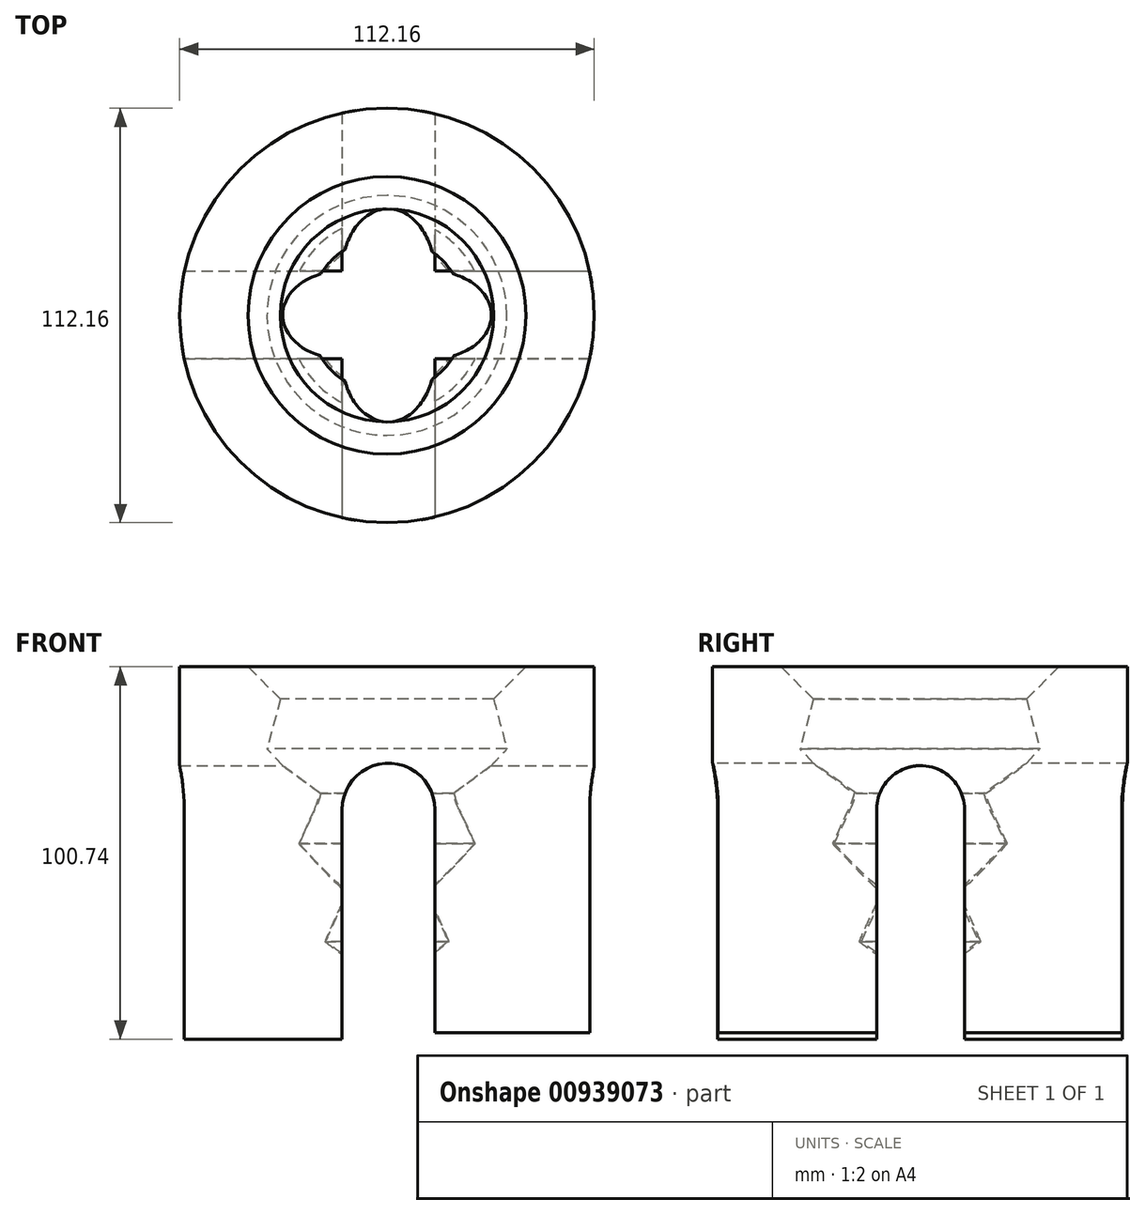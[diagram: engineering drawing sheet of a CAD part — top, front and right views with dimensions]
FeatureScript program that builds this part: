
annotation { "Feature Type Name" : "Feature", "Feature Type Description" : "" }
export const myFeature = defineFeature(function(context is Context, id is Id, definition is map)
    precondition{}
    {
        {
            var Q0;
            Q0=qCreatedBy(makeId("Front.planeOp"),FACE);
            var sketch = newSketch(context, id + "F0", { "sketchPlane" : qUnion([Q0])});
            skLineSegment(sketch, "E0", {"start": v(-15.55, -57.13) * mm, "end": v(0, -57.13) * mm});
            skLineSegment(sketch, "E1", {"start": v(0, -57.13) * mm, "end": v(0, -72.15) * mm});
            skLineSegment(sketch, "E2", {"start": v(0, -72.15) * mm, "end": v(-56.08, -72.15) * mm});
            skLineSegment(sketch, "E3", {"start": v(-56.08, -72.15) * mm, "end": v(-56.08, 38.6) * mm});
            skLineSegment(sketch, "E4", {"start": v(-56.08, 38.6) * mm, "end": v(-37.56, 38.6) * mm});
            skLineSegment(sketch, "E5", {"start": v(-37.56, 38.6) * mm, "end": v(-28.82, 29.87) * mm});
            skLineSegment(sketch, "E6", {"start": v(-28.82, 29.87) * mm, "end": v(-32.45, 16.38) * mm});
            skLineSegment(sketch, "E7", {"start": v(-32.45, 16.38) * mm, "end": v(-21.14, 4.37) * mm});
            skLineSegment(sketch, "E8", {"start": v(-21.14, 4.37) * mm, "end": v(-26.55, -9.26) * mm});
            skLineSegment(sketch, "E9", {"start": v(-26.55, -9.26) * mm, "end": v(-15.9, -22.54) * mm});
            skLineSegment(sketch, "E10", {"start": v(-15.9, -22.54) * mm, "end": v(-20.47, -35.71) * mm});
            skLineSegment(sketch, "E11", {"start": v(-20.47, -35.71) * mm, "end": v(-11.36, -44.55) * mm});
            skLineSegment(sketch, "E12", {"start": v(-11.36, -44.55) * mm, "end": v(-15.55, -57.13) * mm});
            skSolve(sketch);
        }
        {
            var Q0;
            Q0=makeQuery(id+"F0.imprint","IMPRINT",FACE,{"disambiguationData":[TD([[makeQuery(id+"F0.imprint","IMPRINT",EDGE,{"derivedFrom":sQuery(id+"F0.wireOp",EDGE,"E0")}),-1.0]])]});
            var Q1;
            Q1=sQuery(id+"F0.wireOp",EDGE,"E1");
            revolve(context, id + "F1", {"surfaceOperationType" : NewSurfaceOperationType.NEW, "entities" : qUnion([Q0]), "axis" : qUnion([Q1]), "revolveType" : RevolveType.FULL});
        }
        {
            var Q0;
            Q0=qCreatedBy(makeId("Front.planeOp"),FACE);
            var sketch = newSketch(context, id + "F2", { "sketchPlane" : qUnion([Q0])});
            skLineSegment(sketch, "E13", {"start": v(-79.49, -92.5) * mm, "end": v(101.44, -92.5) * mm});
            skLineSegment(sketch, "E14", {"start": v(101.44, -92.5) * mm, "end": v(101.44, -60.37) * mm});
            skLineSegment(sketch, "E15", {"start": v(101.44, -60.37) * mm, "end": v(12.96, -60.37) * mm});
            skLineSegment(sketch, "E16", {"start": v(12.96, -60.37) * mm, "end": v(12.96, 0) * mm});
            skLineSegment(sketch, "E17", {"start": v(12.96, 0) * mm, "end": v(-12.14, 0) * mm});
            skLineSegment(sketch, "E18", {"start": v(-12.14, 0) * mm, "end": v(-12.14, -62.13) * mm});
            skLineSegment(sketch, "E19", {"start": v(-12.14, -62.13) * mm, "end": v(-81.25, -62.13) * mm});
            skLineSegment(sketch, "E20", {"start": v(-81.25, -62.13) * mm, "end": v(-79.49, -92.5) * mm});
            skArc(sketch, "E21", {"start": v(12.96, 0) * mm, "mid": v(0.4, 12.55) * mm, "end": v(-12.14, 0) * mm});
            skSolve(sketch);
        }
        {
            var Q0;
            Q0 = qSketchRegion(id + "F2", true);
            extrude(context, id + "F3", {"entities" : qUnion([Q0]), "operationType" : NewBodyOperationType.REMOVE, "endBound" : BoundingType.THROUGH_ALL, "oppositeDirection" : true, "depth" : 25.4 * mm, "offsetDistance" : 25.4 * mm, "hasSecondDirection" : true, "secondDirectionBound" : SecondDirectionBoundingType.THROUGH_ALL, "secondDirectionOppositeDirection" : false, "secondDirectionDepth" : 25.4 * mm});
        }
        {
            var Q0;
            Q0=qCreatedBy(makeId("Right.planeOp"),FACE);
            var sketch = newSketch(context, id + "F4", { "sketchPlane" : qUnion([Q0])});
            skPoint(sketch, "E22.end.orphan", {"position": v(-11.7, 0) * mm});
            skLineSegment(sketch, "E23", {"start": v(12.05, 0) * mm, "end": v(12.05, -70.05) * mm});
            skLineSegment(sketch, "E24", {"start": v(12.05, -70.05) * mm, "end": v(-11.7, -70.05) * mm});
            skLineSegment(sketch, "E25", {"start": v(-11.7, -70.05) * mm, "end": v(-11.7, 0) * mm});
            skArc(sketch, "E26", {"start": v(12.05, 0) * mm, "mid": v(0.17, 11.88) * mm, "end": v(-11.7, 0) * mm});
            skSolve(sketch);
        }
        {
            var Q0;
            Q0 = qSketchRegion(id + "F4", true);
            extrude(context, id + "F5", {"entities" : qUnion([Q0]), "operationType" : NewBodyOperationType.REMOVE, "endBound" : BoundingType.THROUGH_ALL, "oppositeDirection" : true, "depth" : 25.4 * mm, "offsetDistance" : 25.4 * mm, "hasSecondDirection" : true, "secondDirectionBound" : SecondDirectionBoundingType.THROUGH_ALL, "secondDirectionOppositeDirection" : false, "secondDirectionDepth" : 25.4 * mm});
        }
    });
